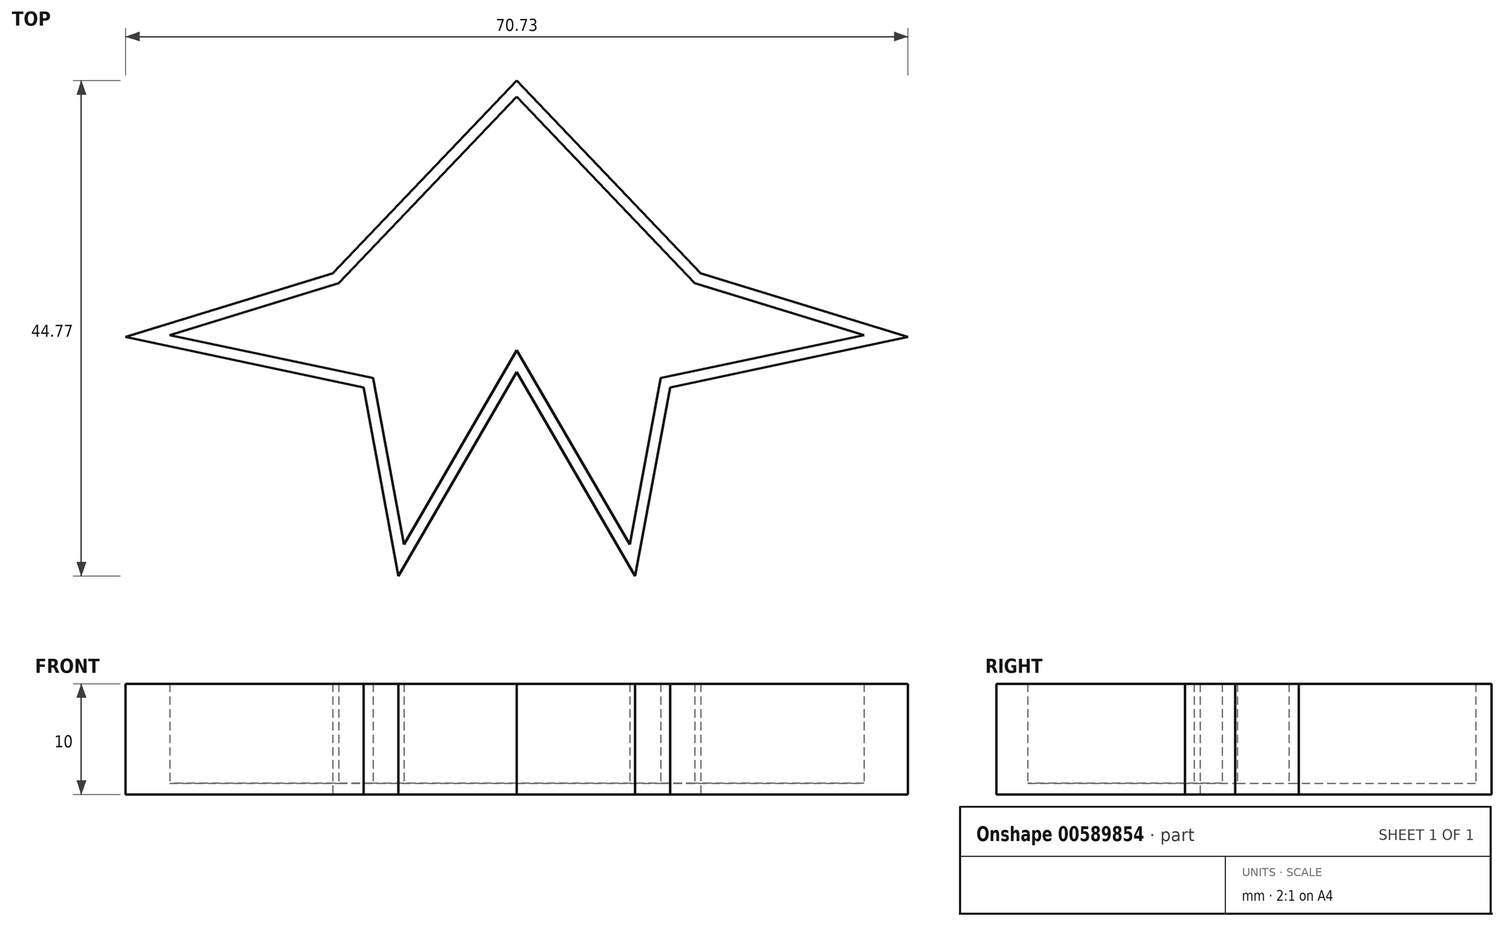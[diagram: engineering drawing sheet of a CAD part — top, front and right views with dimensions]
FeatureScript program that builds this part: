
annotation { "Feature Type Name" : "Feature", "Feature Type Description" : "" }
export const myFeature = defineFeature(function(context is Context, id is Id, definition is map)
    precondition{}
    {
        {
            var Q0;
            Q0=qCreatedBy(makeId("Top.planeOp"),FACE);
            var sketch = newSketch(context, id + "F0", { "sketchPlane" : qUnion([Q0])});
            skLineSegment(sketch, "E0", {"start": v(-35.36, 18.42) * mm, "end": v(-24.67, 0) * mm});
            skLineSegment(sketch, "E1", {"start": v(-24.67, 0) * mm, "end": v(-21.5, 17.04) * mm});
            skLineSegment(sketch, "E2", {"start": v(-21.5, 17.04) * mm, "end": v(0, 21.6) * mm});
            skLineSegment(sketch, "E3", {"start": v(0, 21.6) * mm, "end": v(-18.72, 27.34) * mm});
            skLineSegment(sketch, "E4", {"start": v(-18.72, 27.34) * mm, "end": v(-35.36, 44.77) * mm});
            skPoint(sketch, "E5.orphan", {"position": v(-35.36, 0) * mm});
            skLineSegment(sketch, "E6.MirrorCS", {"start": v(-52, 27.34) * mm, "end": v(-35.36, 44.77) * mm});
            skLineSegment(sketch, "E7.MirrorCS", {"start": v(-70.73, 21.6) * mm, "end": v(-52, 27.34) * mm});
            skLineSegment(sketch, "E8.MirrorCS", {"start": v(-49.23, 17.04) * mm, "end": v(-70.73, 21.6) * mm});
            skLineSegment(sketch, "E9.MirrorCS", {"start": v(-35.36, 18.42) * mm, "end": v(-46.06, 0) * mm});
            skLineSegment(sketch, "E10.MirrorCS", {"start": v(-46.06, 0) * mm, "end": v(-49.23, 17.04) * mm});
            skSolve(sketch);
        }
        {
            var Q0;
            Q0 = qSketchRegion(id + "F0", true);
            extrude(context, id + "F1", {"entities" : qUnion([Q0]), "depth" : 10 * mm, "offsetDistance" : 25 * mm});
        }
        {
            var Q0;
            Q0=makeQuery(id+"F1.opExtrude","CAP_FACE",FACE,{"disambiguationData":[OSD([sQuery(id+"F0.wireOp",EDGE,"E0"),sQuery(id+"F0.wireOp",EDGE,"E1"),sQuery(id+"F0.wireOp",EDGE,"E2"),sQuery(id+"F0.wireOp",EDGE,"E3"),sQuery(id+"F0.wireOp",EDGE,"E4"),sQuery(id+"F0.wireOp",EDGE,"E6.MirrorCS"),sQuery(id+"F0.wireOp",EDGE,"E7.MirrorCS"),sQuery(id+"F0.wireOp",EDGE,"E8.MirrorCS"),sQuery(id+"F0.wireOp",EDGE,"E9.MirrorCS"),sQuery(id+"F0.wireOp",EDGE,"E10.MirrorCS")])],"isStart":false});
            shell(context, id + "F2", {"entities" : qUnion([Q0]), "thickness" : 1 * mm});
        }
    });
